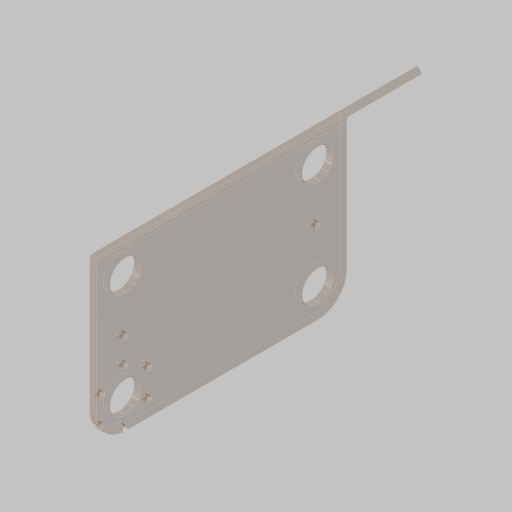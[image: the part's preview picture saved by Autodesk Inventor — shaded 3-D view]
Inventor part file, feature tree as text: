
AUTODESK INVENTOR PART (.ipt)
format: ipt  version: 2023.5 (Build 275446000, 446)  size: 164,352 bytes
history: native  units: in
note: dims shown in document units (in); Inventor stores cm internally (conversion verified against a paired STEP export)
features: sketch x3, sheet_metal_op x3, hole x2, extrude x1, other x1
ambient origin geometry x8: Origin, YZ Plane, XZ Plane, XY Plane, X Axis, Y Axis, Z Axis, Center Point
bodies: Solid1 (feature_tree)
feature tree (10):
  sketch  "Sketch1"  dims[d0=1.125in d2=12.0in]
  extrude  "Extrusion1"  Depth=12.0in
  hole  "Hole1"  [1 undecoded]
  sheet_metal_op  "Flange1"
  hole  "Hole3"  [1 undecoded]
  sketch  "Sketch2"  dims[d3=4.5in d4=3.0in]
  other  "Plate1"
  sheet_metal_op  "Bend1"
  sheet_metal_op  "Corner1"
  sketch  "Sketch4"  dims[d6=0.25in d7=0.5in d8=3.8356in d9=0.25in d10=0.0in d11=0.201in d12=0.38in d13=0.385in d14=0.25in d15=0.5635in d16=1.0in d17=0.8108in d18=0.25in d19=0.25in d20=0.125in d21=0.5in d22=0.25in d23=4.0in d24=45.0deg d25=0.25in d26=1.0in d27=0.25in d28=0.25in d38=2.0in d39=2.3622in d41=360.0deg d43=0.201in d44=0.75in d45=0.385in d46=0.25in d47=0.5635in d48=0.25in d49=0.8108in]
note: 2 required parameter values undecoded (feature->parameter linkage not recoverable at this tier; creation-order binding heuristic only, values carry confidence <= 0.55)
